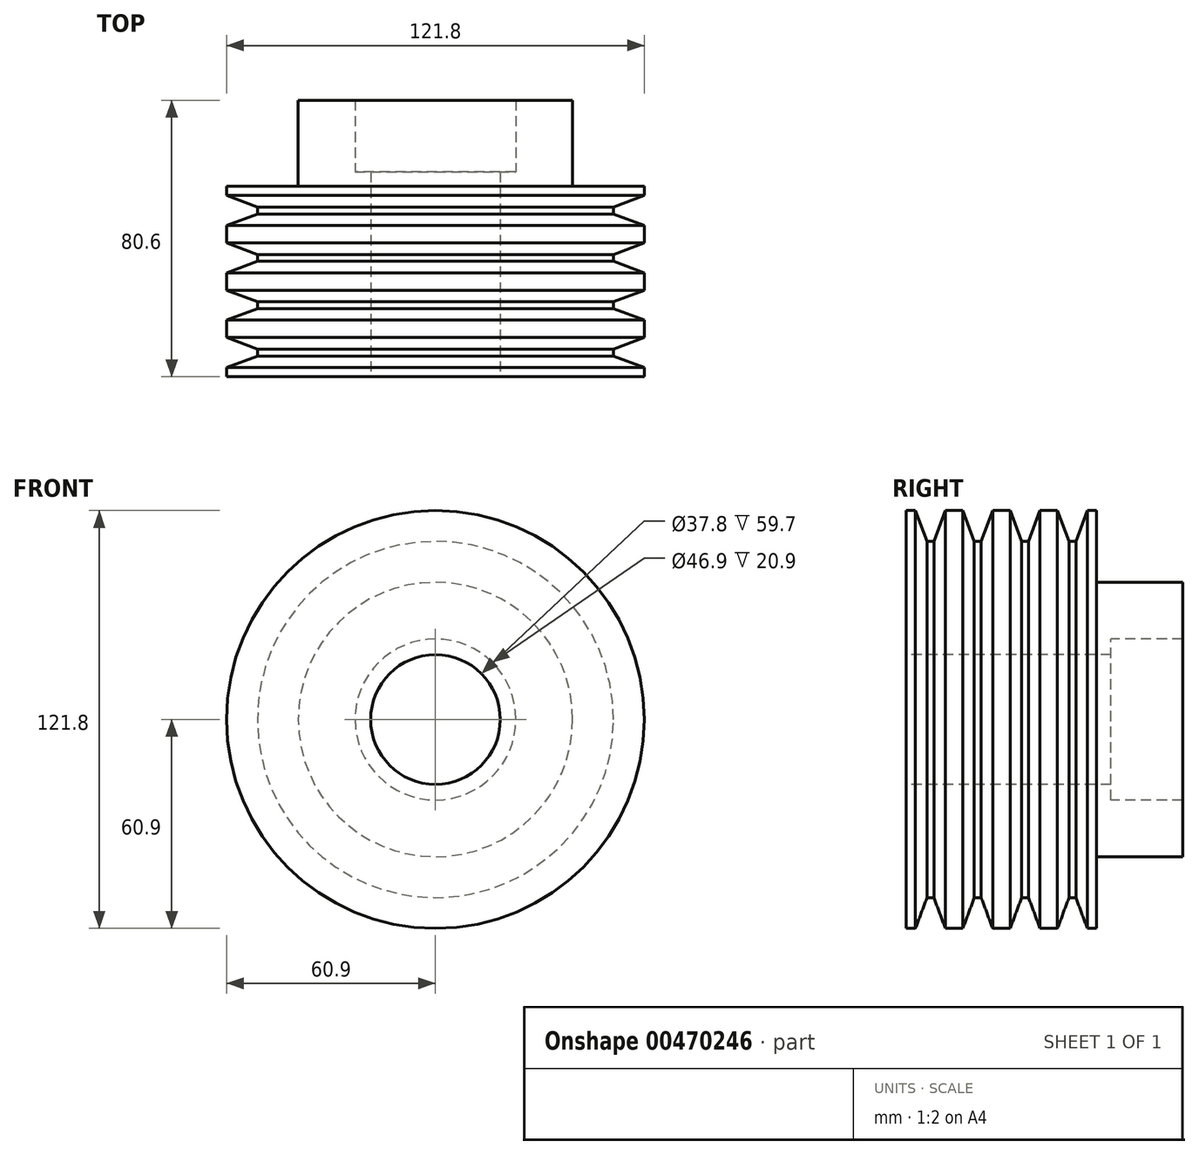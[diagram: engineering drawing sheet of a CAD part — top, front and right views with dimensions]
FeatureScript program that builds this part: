
annotation { "Feature Type Name" : "Feature", "Feature Type Description" : "" }
export const myFeature = defineFeature(function(context is Context, id is Id, definition is map)
    precondition{}
    {
        {
            var Q0;
            Q0=qCreatedBy(makeId("Right.planeOp"),FACE);
            var sketch = newSketch(context, id + "F0", { "sketchPlane" : qUnion([Q0])});
            skLineSegment(sketch, "E0", {"start": v(0, 18.9) * mm, "end": v(0, 60.9) * mm});
            skLineSegment(sketch, "E1", {"start": v(0, 60.9) * mm, "end": v(2.7, 60.9) * mm});
            skLineSegment(sketch, "E2", {"start": v(2.7, 60.9) * mm, "end": v(6.05, 51.9) * mm});
            skLineSegment(sketch, "E3", {"start": v(6.05, 51.9) * mm, "end": v(8.05, 51.9) * mm});
            skLineSegment(sketch, "E4", {"start": v(8.05, 51.9) * mm, "end": v(11.4, 60.9) * mm});
            skLineSegment(sketch, "E5", {"start": v(11.4, 60.9) * mm, "end": v(16.5, 60.9) * mm});
            skLineSegment(sketch, "E6", {"start": v(16.5, 60.9) * mm, "end": v(19.85, 51.9) * mm});
            skLineSegment(sketch, "E7", {"start": v(19.85, 51.9) * mm, "end": v(21.85, 51.9) * mm});
            skLineSegment(sketch, "E8", {"start": v(21.85, 51.9) * mm, "end": v(25.2, 60.9) * mm});
            skLineSegment(sketch, "E9", {"start": v(25.2, 60.9) * mm, "end": v(30.3, 60.9) * mm});
            skLineSegment(sketch, "E10", {"start": v(30.3, 60.9) * mm, "end": v(33.65, 51.9) * mm});
            skLineSegment(sketch, "E11", {"start": v(33.65, 51.9) * mm, "end": v(35.65, 51.9) * mm});
            skLineSegment(sketch, "E12", {"start": v(35.65, 51.9) * mm, "end": v(39, 60.9) * mm});
            skLineSegment(sketch, "E13", {"start": v(39, 60.9) * mm, "end": v(44.1, 60.9) * mm});
            skLineSegment(sketch, "E14", {"start": v(44.1, 60.9) * mm, "end": v(47.45, 51.9) * mm});
            skLineSegment(sketch, "E15", {"start": v(47.45, 51.9) * mm, "end": v(49.45, 51.9) * mm});
            skLineSegment(sketch, "E16", {"start": v(49.45, 51.9) * mm, "end": v(52.8, 60.9) * mm});
            skLineSegment(sketch, "E17", {"start": v(52.8, 60.9) * mm, "end": v(55.5, 60.9) * mm});
            skLineSegment(sketch, "E18", {"start": v(0, 0) * mm, "end": v(80.6, 0) * mm, "construction": true});
            skLineSegment(sketch, "E19", {"start": v(7.05, 51.9) * mm, "end": v(7.05, 60.9) * mm, "construction": true});
            skLineSegment(sketch, "E20", {"start": v(2.7, 60.9) * mm, "end": v(11.4, 60.9) * mm, "construction": true});
            skLineSegment(sketch, "E21", {"start": v(55.5, 40) * mm, "end": v(80.6, 40) * mm});
            skLineSegment(sketch, "E22", {"start": v(55.5, 60.9) * mm, "end": v(55.5, 40) * mm});
            skLineSegment(sketch, "E23", {"start": v(80.6, 40) * mm, "end": v(80.6, 23.45) * mm});
            skLineSegment(sketch, "E24", {"start": v(80.6, 23.45) * mm, "end": v(59.7, 23.45) * mm});
            skLineSegment(sketch, "E25", {"start": v(59.7, 23.45) * mm, "end": v(59.7, 18.9) * mm});
            skLineSegment(sketch, "E26", {"start": v(59.7, 18.9) * mm, "end": v(0, 18.9) * mm});
            skSolve(sketch);
        }
        {
            var Q0;
            Q0=makeQuery(id+"F0.imprint","IMPRINT",FACE,{"disambiguationData":[TD([[makeQuery(id+"F0.imprint","IMPRINT",EDGE,{"derivedFrom":sQuery(id+"F0.wireOp",EDGE,"E0")}),-1.0]])]});
            var Q1;
            Q1=sQuery(id+"F0.wireOp",EDGE,"E18");
            revolve(context, id + "F1", {"entities" : qUnion([Q0]), "axis" : qUnion([Q1]), "revolveType" : RevolveType.FULL});
        }
    });
